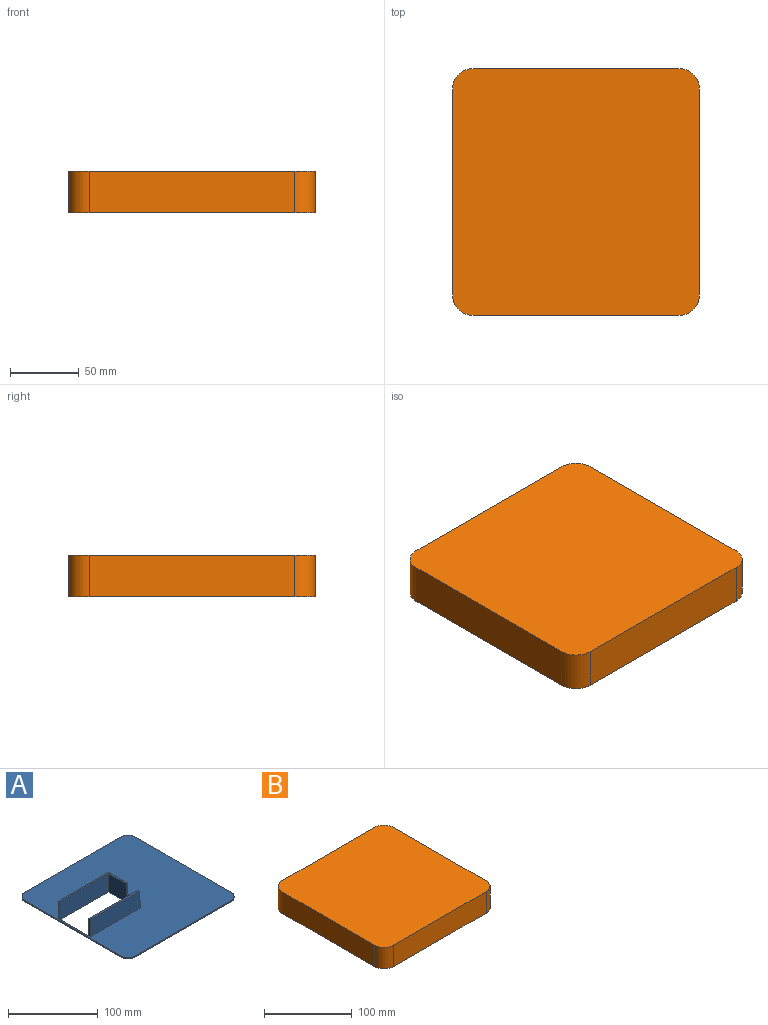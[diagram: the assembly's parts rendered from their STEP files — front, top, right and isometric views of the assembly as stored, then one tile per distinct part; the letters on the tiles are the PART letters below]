
ASSEMBLY  parts=2 mates=1
PART A: 24 faces, bbox 174.6x174.6x25 mm
  f0: plane 14.4x2mm, normal (1,0,0), area 28.8mm2, adj f3,f16,f18,f23
  f1: plane 14.4x2mm, normal (0,-1,0), area 28.8mm2, adj f4,f21,f22,f23
  f2: plane 174.6x174.6mm, normal (0,0,1), area 26370.4mm2, adj f7,f8,f9,f10,f11,f12,f13,f14
  f3: plane 77.37x25mm, normal (0,1,0), area 1934.4mm2, adj f0,f4,f6,f7,f17,f18
  f4: plane 46.2x25mm, normal (-1,0,0), area 897.2mm2, adj f1,f3,f5,f6,f22,f23
  f5: plane 77.37x25mm, normal (0,-1,0), area 1934.4mm2, adj f4,f6,f7,f19,f22
  f6: plane 174.6x174.6mm, normal (0,0,-1), area 26780.3mm2, adj f3,f4,f5,f7,f8,f9,f10,f11
  f7: plane 46.2x1.5mm, normal (1,0,0), area 69.3mm2, adj f2,f3,f5,f6
  f8: plane 150x1.5mm, normal (0,1,0), area 225mm2, adj f2,f6,f9,f15
  f9: cylinder r=12.3mm len=12.3mm, axis (0,0,1), area 29mm2, adj f2,f6,f8,f10
  f10: plane 150x1.5mm, normal (1,0,0), area 225mm2, adj f2,f6,f9,f11
  f11: cylinder r=12.3mm len=12.3mm, axis (0,0,1), area 29mm2, adj f2,f6,f10,f12
  f12: plane 150x1.5mm, normal (0,-1,0), area 225mm2, adj f2,f6,f11,f13
  f13: cylinder r=12.3mm len=12.3mm, axis (0,0,1), area 29mm2, adj f2,f6,f12,f14
  f14: plane 150x1.5mm, normal (-1,0,0), area 225mm2, adj f2,f6,f13,f15
  f15: cylinder r=12.3mm len=12.3mm, axis (0,0,1), area 29mm2, adj f2,f6,f8,f14
  f16: plane 79.37x23.5mm, normal (0,-1,0), area 1836.5mm2, adj f0,f2,f17,f18,f21,f23
  f17: plane 23.5x2mm, normal (-1,0,0), area 47mm2, adj f2,f3,f16,f18
  f18: plane 77.37x2mm, normal (0,0,1), area 154.7mm2, adj f0,f3,f16,f17
  f19: plane 23.5x2mm, normal (-1,0,0), area 47mm2, adj f2,f5,f20,f22
  f20: plane 79.37x23.5mm, normal (0,1,0), area 1865.3mm2, adj f2,f19,f21,f22
  f21: plane 50.2x23.5mm, normal (1,0,0), area 893.1mm2, adj f1,f2,f16,f20,f22,f23
  f22: plane 79.37x30.3mm, normal (0,0,1), area 215.3mm2, adj f1,f4,f5,f19,f20,f21
  f23: plane 19.91x2mm, normal (0,0,1), area 39.8mm2, adj f0,f1,f4,f16,f21
PART B: 44 faces, bbox 180x180x30 mm
  f0: plane 180x180mm, normal (0,0,-1), area 1716mm2, adj f1,f2,f3,f4,f6,f7,f8,f9
  f1: plane 150x30mm, normal (0,1,0), area 4500mm2, adj f0,f5,f6,f9
  f2: plane 150x30mm, normal (-1,0,0), area 4500mm2, adj f0,f5,f6,f7
  f3: plane 150x30mm, normal (0,-1,0), area 4500mm2, adj f0,f5,f7,f8
  f4: plane 150x30mm, normal (1,0,0), area 4500mm2, adj f0,f5,f8,f9
  f5: plane 180x180mm, normal (0,0,1), area 32206.9mm2, adj f1,f2,f3,f4,f6,f7,f8,f9
  f6: cylinder r=15mm len=30mm, axis (0,0,-1), area 706.9mm2, adj f0,f1,f2,f5
  f7: cylinder r=15mm len=30mm, axis (0,0,1), area 706.9mm2, adj f0,f2,f3,f5
  f8: cylinder r=15mm len=30mm, axis (0,0,-1), area 706.9mm2, adj f0,f3,f4,f5
  f9: cylinder r=15mm len=30mm, axis (0,0,1), area 706.9mm2, adj f0,f1,f4,f5
  f10: plane 150x1.5mm, normal (0,-1,0), area 225mm2, adj f0,f14,f17,f18
  f11: plane 150x1.5mm, normal (1,0,0), area 225mm2, adj f0,f14,f15,f18
  f12: plane 150x1.5mm, normal (0,1,0), area 225mm2, adj f0,f15,f16,f18
  f13: plane 150x1.5mm, normal (-1,0,0), area 225mm2, adj f0,f16,f17,f18
  f14: cylinder r=12.5mm len=12.5mm, axis (0,0,-1), area 29.5mm2, adj f0,f10,f11,f18
  f15: cylinder r=12.5mm len=12.5mm, axis (0,0,1), area 29.5mm2, adj f0,f11,f12,f18
  f16: cylinder r=12.5mm len=12.5mm, axis (0,0,-1), area 29.5mm2, adj f0,f12,f13,f18
  f17: cylinder r=12.5mm len=12.5mm, axis (0,0,1), area 29.5mm2, adj f0,f10,f13,f18
  f18: plane 175x175mm, normal (0,0,-1), area 1676.7mm2, adj f10,f11,f12,f13,f14,f15,f16,f17
  f19: plane 150x25.5mm, normal (0,-1,0), area 3825mm2, adj f18,f20,f26,f27
  f20: cylinder r=10mm len=25.5mm, axis (0,0,1), area 400.6mm2, adj f18,f19,f21,f27
  f21: plane 150x25.5mm, normal (-1,0,0), area 3825mm2, adj f18,f20,f22,f27
  f22: cylinder r=10mm len=25.5mm, axis (0,0,1), area 400.6mm2, adj f18,f21,f23,f27
  f23: plane 150x25.5mm, normal (0,1,0), area 3825mm2, adj f18,f22,f24,f27
  f24: cylinder r=10mm len=25.5mm, axis (0,0,1), area 400.6mm2, adj f18,f23,f25,f27
  f25: plane 150x25.5mm, normal (1,0,0), area 3825mm2, adj f18,f24,f26,f27
  f26: cylinder r=10mm len=25.5mm, axis (0,0,1), area 400.6mm2, adj f18,f19,f25,f27
  f27: plane 170x170mm, normal (0,0,-1), area 28434mm2, adj f19,f20,f21,f22,f23,f24,f25,f26
  f28: plane 5x5mm, normal (0,0,-1), area 16.5mm2, adj f38,f40
  f29: plane 5x5mm, normal (0,0,-1), area 16.5mm2, adj f36,f43
  f30: plane 5x5mm, normal (0,0,-1), area 16.5mm2, adj f34,f42
  f31: plane 5x5mm, normal (0,0,-1), area 16.5mm2, adj f32,f41
  f32: cylinder r=1mm len=3.5mm, axis (0,0,1), area 22mm2, adj f31,f33
  f33: plane 2x2mm, normal (0,0,-1), area 3.1mm2, adj f32
  f34: cylinder r=1mm len=3.5mm, axis (0,0,1), area 22mm2, adj f30,f35
  f35: plane 2x2mm, normal (0,0,-1), area 3.1mm2, adj f34
  f36: cylinder r=1mm len=3.5mm, axis (0,0,1), area 22mm2, adj f29,f37
  f37: plane 2x2mm, normal (0,0,-1), area 3.1mm2, adj f36
  f38: cylinder r=1mm len=3.5mm, axis (0,0,1), area 22mm2, adj f28,f39
  f39: plane 2x2mm, normal (0,0,-1), area 3.1mm2, adj f38
  f40: cone r=5.5mm half-angle=45deg, axis (0,0,1), area 106.6mm2, adj f27,f28
  f41: cone r=5.5mm half-angle=45deg, axis (0,0,1), area 106.6mm2, adj f27,f31
  f42: cone r=5.5mm half-angle=45deg, axis (0,0,1), area 106.6mm2, adj f27,f30
  f43: cone r=5.5mm half-angle=45deg, axis (0,0,1), area 106.6mm2, adj f27,f29
PLACE A t=(72.01,-13.32,63.85)mm
PLACE B t=(72.01,-13.52,63.85)mm
MATE fastened A.f8 <-> B.f10  axis (0,1,0) through (77.01,133.98,56.2)mm
